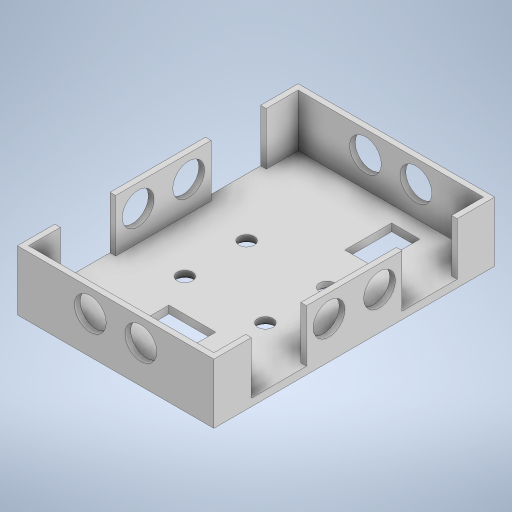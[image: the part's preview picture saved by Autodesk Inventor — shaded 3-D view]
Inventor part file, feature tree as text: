
AUTODESK INVENTOR PART (.ipt)
format: ipt  version: 2024.2 (Build 282272000, 272)  size: 442,368 bytes
history: native  units: mm
features: extrude x9, sketch x9, chamfer x1
ambient origin geometry x8: Origin, YZ Plane, XZ Plane, XY Plane, X Axis, Y Axis, Z Axis, Center Point
bodies: Solid1 (feature_tree)
feature tree (19):
  extrude  "Extrusion1"  Depth=48.0mm
  extrude  "Extrusion3"  Depth=4.7mm
  extrude  "Extrusion4"  Depth=4.7mm
  extrude  "remove legs"  Depth=43.0mm
  extrude  "Extrusion6"  Depth=7.5mm
  extrude  "Extrusion7"  Depth=7.5mm
  chamfer  "Chamfer1"  Distance=10.0mm
  sketch  "Sketch7"  dims[d12=7.500001mm]
  sketch  "Sketch8"  dims[d13=7.500001mm]
  sketch  "Sketch9"  dims[d14=10.0mm d15=10.0mm d16=10.0mm d17=10.0mm d18=12.0mm d19=0.0mm d20=105.0mm d21=150.0mm d22=58.5mm d23=31.0mm d26=4.0mm d27=0.0mm d28=20.0mm d45=28.0mm d46=0.0mm d48=20.0mm d49=3.0mm d50=3.0mm d51=3.0mm d52=3.0mm d53=20.0mm d55=20.0mm d56=20.0mm d57=3.0mm d59=100.0mm d60=15.0mm d61=25.0mm d62=0.0mm d63=8.2mm d64=8.2mm d65=8.2mm d66=8.2mm d67=4.0mm d68=0.0mm d69=20.0mm d72=25.0mm d73=15.0mm d74=15.0mm d75=25.0mm d76=22.0mm d77=2.5mm d78=9.0mm d79=17.5mm d80=10.0mm d81=0.0mm d82=1.0mm d83=2.0mm d84=45.0deg d88=3.0mm d89=51.0mm d91=3.0mm d92=51.0mm d95=17.0mm d96=65.0mm d102=3.0mm d103=17.0mm d104=65.0mm d105=17.0mm d106=17.0mm d107=17.0mm d108=27.0mm d109=20.0mm d113=17.0mm d114=17.0mm d115=20.0mm d116=49.5mm d117=28.0mm d118=0.0mm d119=61.5mm d120=0.0mm d121=0.0mm d122=0.0mm d123=0.0mm d124=20.0mm d125=39.0mm d126=27.0mm]
  extrude  "Extrusion10"  Depth=10.0mm
  extrude  "Extrusion11"  Depth=10.0mm
  extrude  "Extrusion12"  Depth=20.0mm TaperAngle=0.0deg
  sketch  "Sketch1"  dims[d0=58.0mm d1=48.0mm]
  sketch  "Sketch2"  dims[d2=4.7mm d3=4.7mm]
  sketch  "Sketch3"  dims[d4=4.7mm d5=4.7mm]
  sketch  "Sketch4"  dims[d6=33.0mm d7=43.0mm]
  sketch  "Sketch5"  dims[d8=7.5mm d9=7.5mm]
  sketch  "Sketch6"  dims[d10=7.5mm d11=7.5mm]
